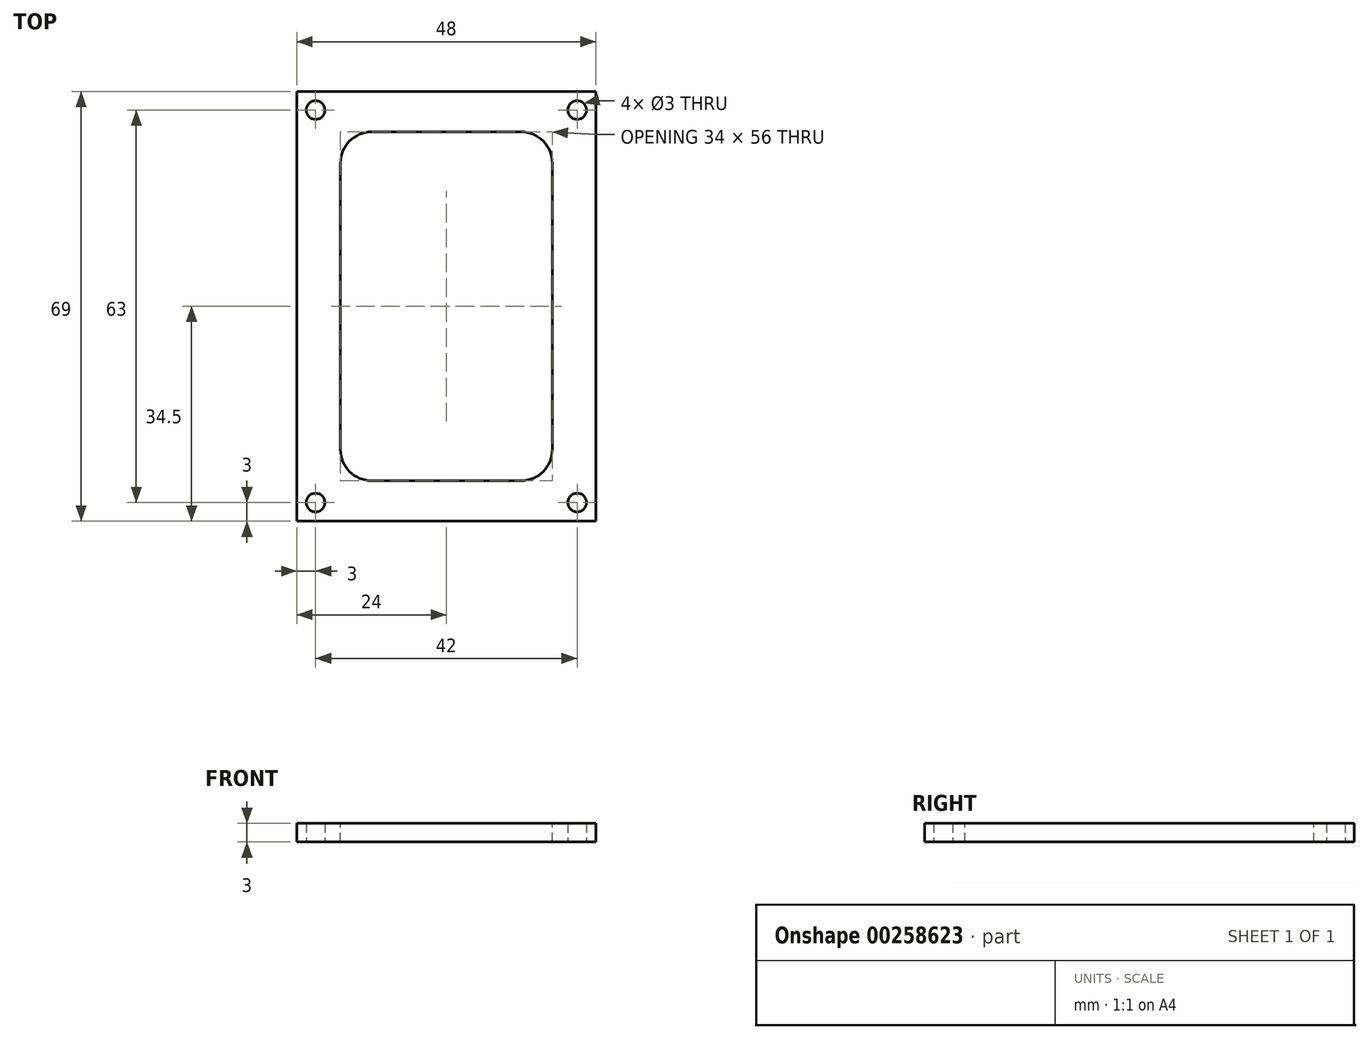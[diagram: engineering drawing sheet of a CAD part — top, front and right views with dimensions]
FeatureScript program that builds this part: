
annotation { "Feature Type Name" : "Feature", "Feature Type Description" : "" }
export const myFeature = defineFeature(function(context is Context, id is Id, definition is map)
    precondition{}
    {
        {
            var Q0;
            Q0=qCreatedBy(makeId("Top.planeOp"),FACE);
            var sketch = newSketch(context, id + "F0", { "sketchPlane" : qUnion([Q0])});
            skLineSegment(sketch, "E0.bottom", {"start": v(24, 34.5) * mm, "end": v(-24, 34.5) * mm});
            skLineSegment(sketch, "E0.top", {"start": v(24, -34.5) * mm, "end": v(-24, -34.5) * mm});
            skLineSegment(sketch, "E0.left", {"start": v(24, 34.5) * mm, "end": v(24, -34.5) * mm});
            skLineSegment(sketch, "E0.right", {"start": v(-24, 34.5) * mm, "end": v(-24, -34.5) * mm});
            skPoint(sketch, "E0.middle", {"position": v(0, 0) * mm});
            skCircle(sketch, "E1", {"center": v(-21, 31.5) * mm, "radius": 1.5 * mm});
            skCircle(sketch, "E2.MirrorC", {"center": v(21, 31.5) * mm, "radius": 1.5 * mm});
            skCircle(sketch, "E3", {"center": v(-21, -31.5) * mm, "radius": 1.5 * mm});
            skCircle(sketch, "E4.MirrorC", {"center": v(21, -31.5) * mm, "radius": 1.5 * mm});
            skSolve(sketch);
        }
        {
            var Q0;
            Q0=qSketchRegion(id+"F0",true);
            extrude(context, id + "F1", {"entities" : qUnion([Q0]), "depth" : 3 * mm});
        }
        {
            var Q0;
            Q0=makeQuery(id+"F1.opExtrude","CAP_FACE",FACE,{"disambiguationData":[OSD([sQuery(id+"F0.wireOp",EDGE,"E0.bottom"),sQuery(id+"F0.wireOp",EDGE,"E0.top"),sQuery(id+"F0.wireOp",EDGE,"E0.left"),sQuery(id+"F0.wireOp",EDGE,"E0.right"),sQuery(id+"F0.wireOp",EDGE,"E1"),sQuery(id+"F0.wireOp",EDGE,"E2.MirrorC"),sQuery(id+"F0.wireOp",EDGE,"E3"),sQuery(id+"F0.wireOp",EDGE,"E4.MirrorC")])],"isStart":false});
            var sketch = newSketch(context, id + "F2", { "sketchPlane" : qUnion([Q0])});
            skLineSegment(sketch, "E5.bottom", {"start": v(-17, 28) * mm, "end": v(17, 28) * mm});
            skLineSegment(sketch, "E5.top", {"start": v(-17, -28) * mm, "end": v(17, -28) * mm});
            skLineSegment(sketch, "E5.left", {"start": v(-17, 28) * mm, "end": v(-17, -28) * mm});
            skLineSegment(sketch, "E5.right", {"start": v(17, 28) * mm, "end": v(17, -28) * mm});
            skPoint(sketch, "E5.middle", {"position": v(0, 0) * mm});
            skSolve(sketch);
        }
        {
            var Q0;
            Q0=qSketchRegion(id+"F2",true);
            extrude(context, id + "F3", {"entities" : qUnion([Q0]), "operationType" : NewBodyOperationType.REMOVE, "endBound" : BoundingType.UP_TO_NEXT, "oppositeDirection" : true, "depth" : 25 * mm});
        }
        {
            var Q0;
            Q0=makeQuery(id+"F3.boolean.opBoolean","COPY",EDGE,{"derivedFrom":makeQuery(id+"F3.opExtrude","SWEPT_EDGE",EDGE,{"disambiguationData":[OSD([sQuery(id+"F2.wireOp",EDGE,"E5.bottom"),sQuery(id+"F2.wireOp",EDGE,"E5.left")])]})});
            fillet(context, id + "F4", {"entities" : qUnion([Q0]), "radius" : 5 * mm, "tangentPropagation" : true, "allowEdgeOverflow" : false});
        }
        {
            var Q0;
            Q0=makeQuery(id+"F3.boolean.opBoolean","COPY",EDGE,{"derivedFrom":makeQuery(id+"F3.opExtrude","SWEPT_EDGE",EDGE,{"disambiguationData":[OSD([sQuery(id+"F2.wireOp",EDGE,"E5.top"),sQuery(id+"F2.wireOp",EDGE,"E5.left")])]})});
            var Q1;
            Q1=makeQuery(id+"F3.boolean.opBoolean","COPY",EDGE,{"derivedFrom":makeQuery(id+"F3.opExtrude","SWEPT_EDGE",EDGE,{"disambiguationData":[OSD([sQuery(id+"F2.wireOp",EDGE,"E5.top"),sQuery(id+"F2.wireOp",EDGE,"E5.right")])]})});
            var Q2;
            Q2=makeQuery(id+"F3.boolean.opBoolean","COPY",EDGE,{"derivedFrom":makeQuery(id+"F3.opExtrude","SWEPT_EDGE",EDGE,{"disambiguationData":[OSD([sQuery(id+"F2.wireOp",EDGE,"E5.bottom"),sQuery(id+"F2.wireOp",EDGE,"E5.right")])]})});
            fillet(context, id + "F5", {"entities" : qUnion([Q0, Q1, Q2]), "radius" : 5 * mm, "tangentPropagation" : true, "allowEdgeOverflow" : false});
        }
    });
